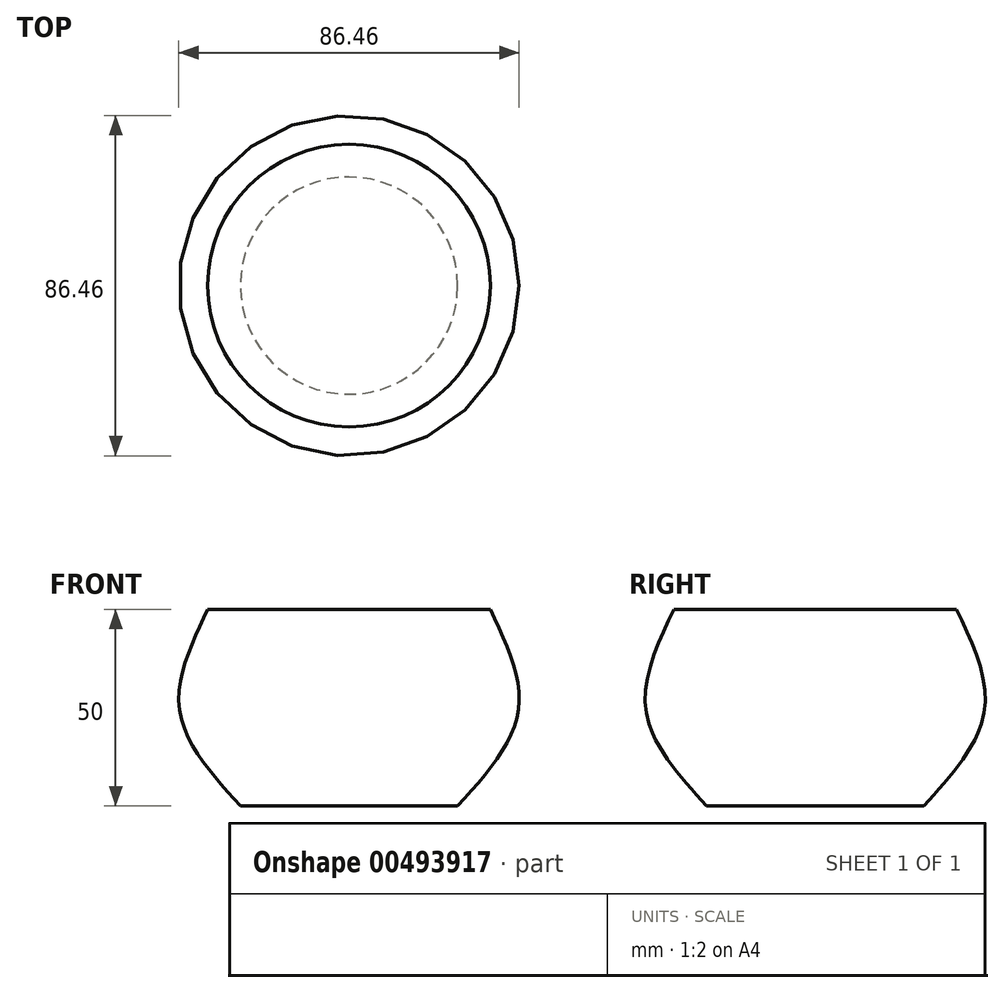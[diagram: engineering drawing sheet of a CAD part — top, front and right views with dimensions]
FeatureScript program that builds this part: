
annotation { "Feature Type Name" : "Feature", "Feature Type Description" : "" }
export const myFeature = defineFeature(function(context is Context, id is Id, definition is map)
    precondition{}
    {
        {
            var Q0;
            Q0=qCreatedBy(makeId("Top.planeOp"),FACE);
            cPlane(context, id + "F0", {"entities" : qUnion([Q0]), "cplaneType" : CPlaneType.OFFSET, "offset" : 25 * mm, "width" : 150 * mm, "height" : 150 * mm});
        }
        {
            var Q0;
            Q0=qCreatedBy(id+"F0.planeOp",FACE);
            cPlane(context, id + "F1", {"entities" : qUnion([Q0]), "cplaneType" : CPlaneType.OFFSET, "offset" : 25 * mm, "width" : 150 * mm, "height" : 150 * mm});
        }
        {
            var Q0;
            Q0=qCreatedBy(makeId("Top.planeOp"),FACE);
            var sketch = newSketch(context, id + "F2", { "sketchPlane" : qUnion([Q0])});
            skCircle(sketch, "E0", {"center": v(0, 0) * mm, "radius": 27.6 * mm});
            skSolve(sketch);
        }
        {
            var Q0;
            Q0=qCreatedBy(id+"F0.planeOp",FACE);
            var sketch = newSketch(context, id + "F3", { "sketchPlane" : qUnion([Q0])});
            skCircle(sketch, "E1", {"center": v(0, 0) * mm, "radius": 43.11 * mm});
            skSolve(sketch);
        }
        {
            var Q0;
            Q0=qCreatedBy(id+"F1.planeOp",FACE);
            var sketch = newSketch(context, id + "F4", { "sketchPlane" : qUnion([Q0])});
            skCircle(sketch, "E2", {"center": v(0, 0) * mm, "radius": 35.9 * mm});
            skSolve(sketch);
        }
        {
            var Q0;
            Q0=makeQuery(id+"F2.imprint","IMPRINT",FACE,{"disambiguationData":[TD([[makeQuery(id+"F2.imprint","IMPRINT",EDGE,{"derivedFrom":sQuery(id+"F2.wireOp",EDGE,"E0")}),1.0]])]});
            var Q1;
            Q1=makeQuery(id+"F3.imprint","IMPRINT",FACE,{"disambiguationData":[TD([[makeQuery(id+"F3.imprint","IMPRINT",EDGE,{"derivedFrom":sQuery(id+"F3.wireOp",EDGE,"E1")}),1.0]])]});
            var Q2;
            Q2=makeQuery(id+"F4.imprint","IMPRINT",FACE,{"disambiguationData":[TD([[makeQuery(id+"F4.imprint","IMPRINT",EDGE,{"derivedFrom":sQuery(id+"F4.wireOp",EDGE,"E2")}),1.0]])]});
            loft(context, id + "F5", {"sheetProfilesArray" : [{ "sheetProfileEntities" : qUnion([Q0]) }, { "sheetProfileEntities" : qUnion([Q1]) }, { "sheetProfileEntities" : qUnion([Q2]) }]});
        }
    });
